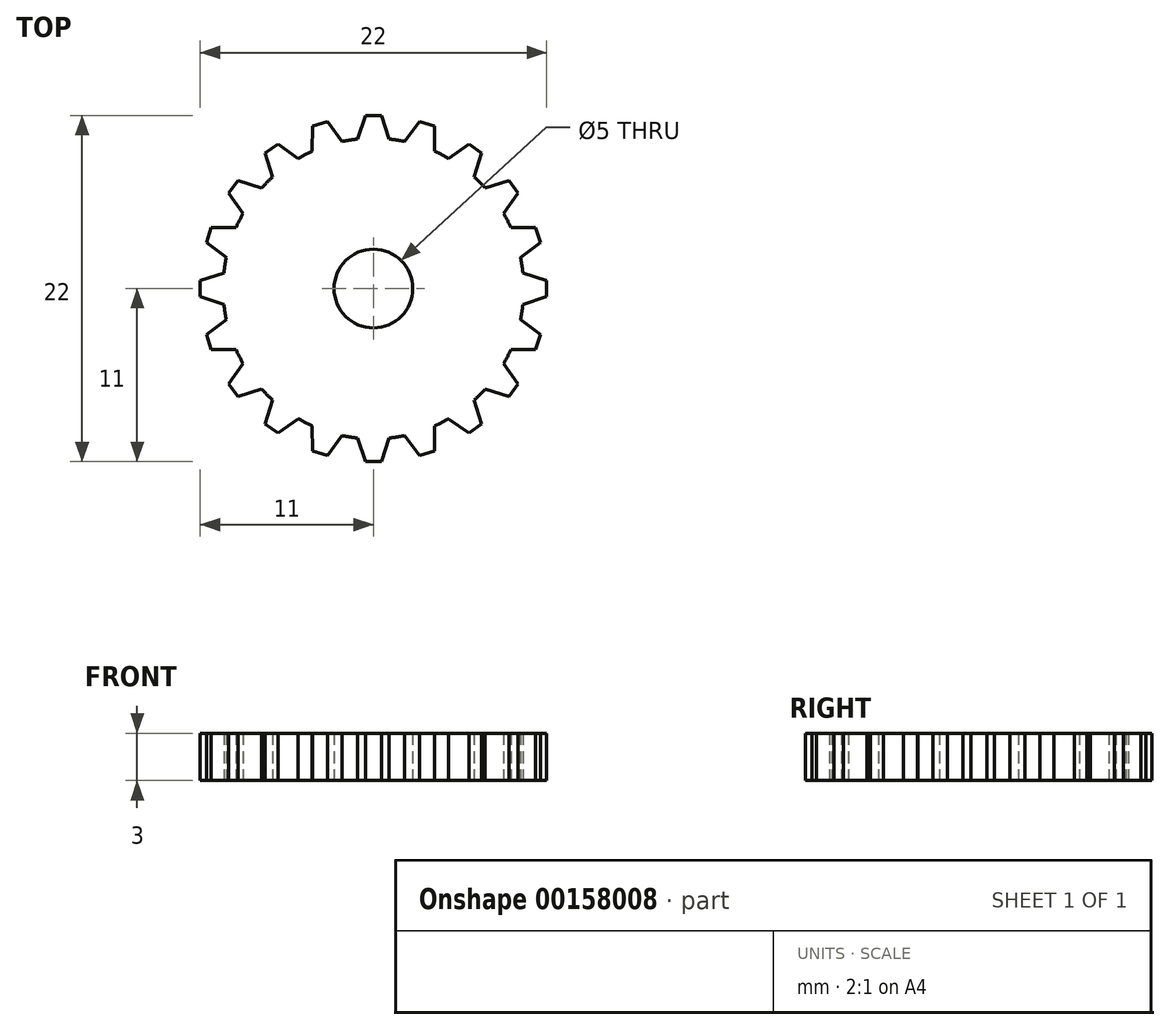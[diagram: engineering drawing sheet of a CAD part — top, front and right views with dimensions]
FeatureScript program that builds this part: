
annotation { "Feature Type Name" : "Feature", "Feature Type Description" : "" }
export const myFeature = defineFeature(function(context is Context, id is Id, definition is map)
    precondition{}
    {
        {
            var Q0;
            Q0=qCreatedBy(makeId("Top.planeOp"),FACE);
            var sketch = newSketch(context, id + "F0", { "sketchPlane" : qUnion([Q0])});
            skCircle(sketch, "E0", {"center": v(0, 0) * mm, "radius": 9.55 * mm});
            skCircle(sketch, "E1", {"center": v(0, 0) * mm, "radius": 2.5 * mm});
            skSolve(sketch);
        }
        {
            var Q0;
            Q0=makeQuery(id+"F0.imprint","IMPRINT",FACE,{"disambiguationData":[TD([[makeQuery(id+"F0.imprint","IMPRINT",EDGE,{"derivedFrom":sQuery(id+"F0.wireOp",EDGE,"E0")}),1.0]])]});
            var sketch = newSketch(context, id + "F1", { "sketchPlane" : qUnion([Q0])});
            skCircle(sketch, "E2.0", {"center": v(0, 0) * mm, "radius": 9.55 * mm});
            skLineSegment(sketch, "E3", {"start": v(-1, 9.5) * mm, "end": v(-0.5, 11) * mm});
            skLineSegment(sketch, "E4", {"start": v(-0.5, 11) * mm, "end": v(0.5, 11) * mm});
            skLineSegment(sketch, "E5", {"start": v(0.5, 11) * mm, "end": v(1, 9.5) * mm});
            skSolve(sketch);
        }
        {
            var Q0;
            Q0=makeQuery(id+"F0.imprint","IMPRINT",FACE,{"disambiguationData":[TD([[makeQuery(id+"F0.imprint","IMPRINT",EDGE,{"derivedFrom":sQuery(id+"F0.wireOp",EDGE,"E0")}),1.0]])]});
            var Q1;
            {var subQ0=sQuery(id+"F1.wireOp",EDGE,"E3");Q1=makeQuery(id+"F1.imprint","IMPRINT",FACE,{"disambiguationData":[TD([[makeQuery(id+"F1.imprint","IMPRINT",EDGE,{"derivedFrom":subQ0}),-1.0]])]});}
            extrude(context, id + "F2", {"entities" : qUnion([Q0, Q1]), "depth" : 3 * mm});
        }
        {
            var Q0;
            Q0=makeQuery(id+"F2.opExtrude","SWEPT_BODY",BODY,{"disambiguationData":[OSD([sQuery(id+"F1.wireOp",EDGE,"E2.0"),sQuery(id+"F1.wireOp",EDGE,"E3"),sQuery(id+"F1.wireOp",EDGE,"E4"),sQuery(id+"F1.wireOp",EDGE,"E5")])]});
            var Q1;
            Q1=makeQuery(id+"F2.opExtrude","CAP_EDGE",EDGE,{"disambiguationData":[OSD([sQuery(id+"F0.wireOp",EDGE,"E0")])],"isStart":false});
            circularPattern(context, id + "F3", {"operationType" : NewBodyOperationType.ADD, "entities" : qUnion([Q0]), "axis" : qUnion([Q1]), "angle" : 18 * degree, "instanceCount" : 20});
        }
    });
